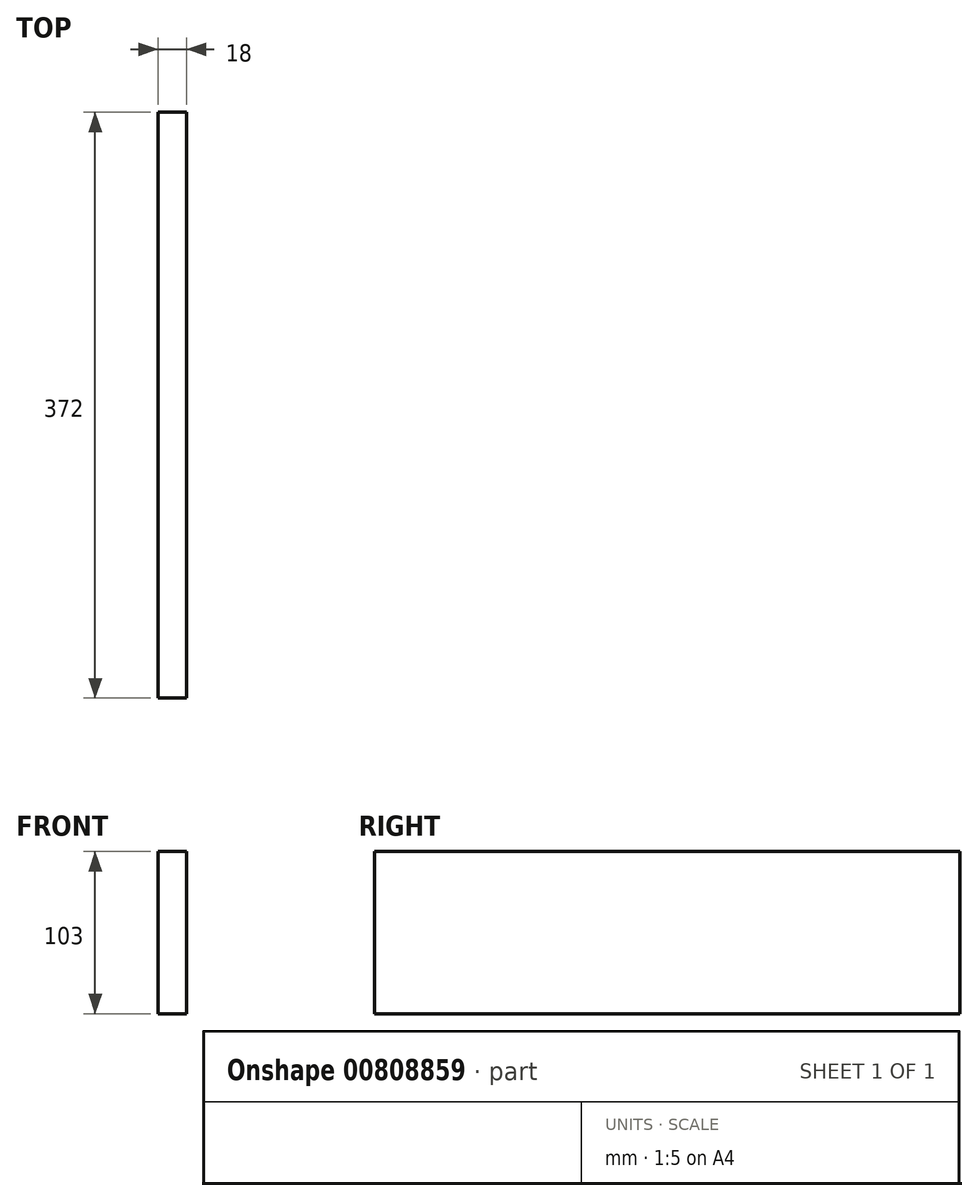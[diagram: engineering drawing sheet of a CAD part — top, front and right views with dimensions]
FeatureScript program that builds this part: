
annotation { "Feature Type Name" : "Feature", "Feature Type Description" : "" }
export const myFeature = defineFeature(function(context is Context, id is Id, definition is map)
    precondition{}
    {
        {
            var Q0;
            Q0=qCreatedBy(makeId("Right.planeOp"),FACE);
            var sketch = newSketch(context, id + "F0", { "sketchPlane" : qUnion([Q0])});
            skLineSegment(sketch, "E0.bottom", {"start": v(0, 0) * mm, "end": v(372, 0) * mm});
            skLineSegment(sketch, "E0.top", {"start": v(0, 103) * mm, "end": v(372, 103) * mm});
            skLineSegment(sketch, "E0.left", {"start": v(0, 0) * mm, "end": v(0, 103) * mm});
            skLineSegment(sketch, "E0.right", {"start": v(372, 0) * mm, "end": v(372, 103) * mm});
            skSolve(sketch);
        }
        {
            var Q0;
            Q0=makeQuery(id+"F0.imprint","IMPRINT",FACE,{"disambiguationData":[TD([[makeQuery(id+"F0.imprint","IMPRINT",EDGE,{"derivedFrom":sQuery(id+"F0.wireOp",EDGE,"E0.bottom")}),1.0]])]});
            var Q1;
            Q1=sQuery(id+"F0.wireOp",EDGE,"E0.top");
            var Q2;
            Q2=sQuery(id+"F0.wireOp",EDGE,"E0.left");
            var Q3;
            Q3=sQuery(id+"F0.wireOp",EDGE,"E0.right");
            var Q4;
            Q4=sQuery(id+"F0.wireOp",EDGE,"E0.bottom");
            extrude(context, id + "F1", {"entities" : qUnion([Q0]), "surfaceEntities" : qUnion([Q1, Q2, Q3, Q4]), "depth" : 18 * mm, "offsetDistance" : 25 * mm});
        }
    });
